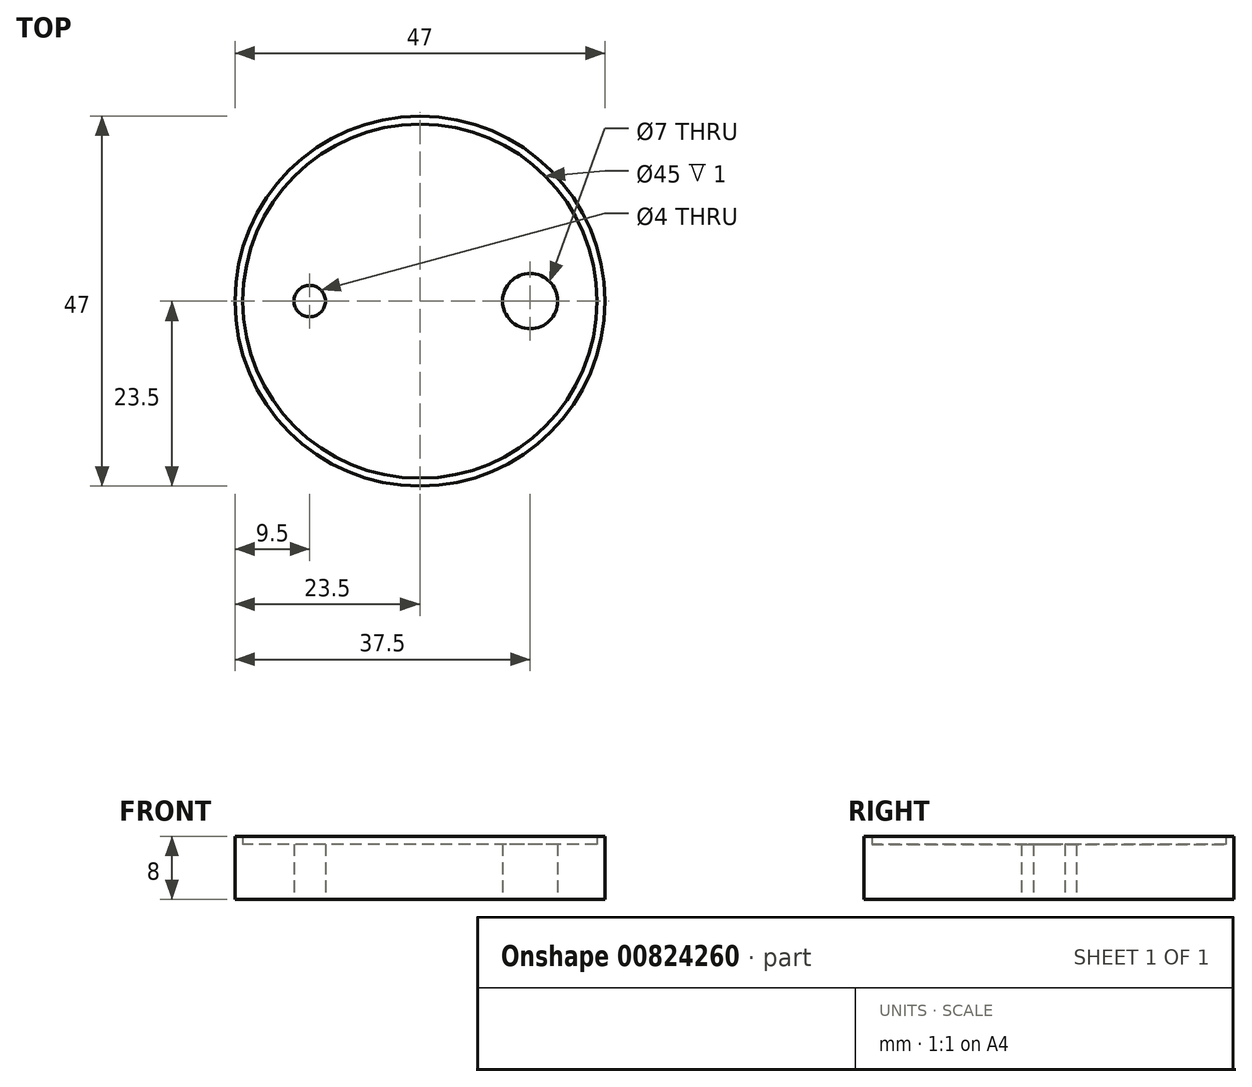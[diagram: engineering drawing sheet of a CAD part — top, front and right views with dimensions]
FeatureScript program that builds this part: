
annotation { "Feature Type Name" : "Feature", "Feature Type Description" : "" }
export const myFeature = defineFeature(function(context is Context, id is Id, definition is map)
    precondition{}
    {
        {
            var Q0;
            Q0=qCreatedBy(makeId("Top.planeOp"),FACE);
            var sketch = newSketch(context, id + "F0", { "sketchPlane" : qUnion([Q0])});
            skCircle(sketch, "E0", {"center": v(0, 0) * mm, "radius": 20 * mm});
            skCircle(sketch, "E1", {"center": v(0, 0) * mm, "radius": 22.5 * mm});
            skCircle(sketch, "E2", {"center": v(0, 0) * mm, "radius": 23.5 * mm});
            skPoint(sketch, "E3", {"position": v(-14, 0) * mm});
            skCircle(sketch, "E4", {"center": v(-14, 0) * mm, "radius": 3.5 * mm});
            skCircle(sketch, "E5.MirrorC", {"center": v(14, 0) * mm, "radius": 3.5 * mm});
            skLineSegment(sketch, "E6", {"start": v(-14, 3.5) * mm, "end": v(-19.7, 3.5) * mm});
            skLineSegment(sketch, "E7", {"start": v(-14, -3.5) * mm, "end": v(-19.7, -3.5) * mm});
            skLineSegment(sketch, "E8.MirrorCS", {"start": v(14, 3.5) * mm, "end": v(19.7, 3.5) * mm});
            skLineSegment(sketch, "E9.MirrorCS", {"start": v(14, -3.5) * mm, "end": v(19.7, -3.5) * mm});
            skSolve(sketch);
        }
        {
            var Q0;
            Q0=makeQuery(id+"F0.imprint","IMPRINT",FACE,{"disambiguationData":[TD([[makeQuery(id+"F0.imprint","IMPRINT",EDGE,{"derivedFrom":sQuery(id+"F0.wireOp",EDGE,"E1")}),1.0]])]});
            var Q1;
            {var subQ0=sQuery(id+"F0.wireOp",EDGE,"E6");Q1=makeQuery(id+"F0.imprint","IMPRINT",FACE,{"disambiguationData":[TD([[makeQuery(id+"F0.imprint","IMPRINT",EDGE,{"derivedFrom":subQ0}),1.0]])]});}
            var Q2;
            {var subQ0=sQuery(id+"F0.wireOp",EDGE,"E4");var subQ1=makeQuery(id+"F0.imprint","INTERSECT",VERTEX,{"derivedFrom":[subQ0,sQuery(id+"F0.wireOp",EDGE,"E6")]});Q2=makeQuery(id+"F0.imprint","IMPRINT",FACE,{"disambiguationData":[TD([[makeQuery(id+"F0.imprint","IMPRINT",EDGE,{"disambiguationData":[TD([[subQ1,-1.0]])],"derivedFrom":subQ0}),1.0]])]});}
            var Q3;
            {var subQ0=sQuery(id+"F0.wireOp",EDGE,"E5.MirrorC");var subQ1=makeQuery(id+"F0.imprint","INTERSECT",VERTEX,{"derivedFrom":[subQ0,sQuery(id+"F0.wireOp",EDGE,"E8.MirrorCS")]});Q3=makeQuery(id+"F0.imprint","IMPRINT",FACE,{"disambiguationData":[TD([[makeQuery(id+"F0.imprint","IMPRINT",EDGE,{"disambiguationData":[TD([[subQ1,-1.0]])],"derivedFrom":subQ0}),-1.0]])]});}
            var Q4;
            {var subQ0=sQuery(id+"F0.wireOp",EDGE,"E8.MirrorCS");Q4=makeQuery(id+"F0.imprint","IMPRINT",FACE,{"disambiguationData":[TD([[makeQuery(id+"F0.imprint","IMPRINT",EDGE,{"derivedFrom":subQ0}),-1.0]])]});}
            extrude(context, id + "F1", {"entities" : qUnion([Q0, Q1, Q2, Q3, Q4]), "depth" : 7 * mm, "offsetDistance" : 25 * mm});
        }
        {
            var Q0;
            Q0=makeQuery(id+"F0.imprint","IMPRINT",FACE,{"disambiguationData":[TD([[makeQuery(id+"F0.imprint","IMPRINT",EDGE,{"derivedFrom":sQuery(id+"F0.wireOp",EDGE,"E1")}),-1.0]])]});
            extrude(context, id + "F2", {"entities" : qUnion([Q0]), "operationType" : NewBodyOperationType.ADD, "depth" : 8 * mm, "offsetDistance" : 25 * mm});
        }
        {
            var Q0;
            Q0=sQuery(id+"F0.wireOp",VERTEX,"E3");
            var Q1;
            Q1=sQuery(id+"F0.wireOp",VERTEX,"E5.MirrorC.center");
            var Q2;
            Q2=makeQuery(id+"F1.opExtrude","SWEPT_BODY",BODY,{"disambiguationData":[OSD([sQuery(id+"F0.wireOp",EDGE,"E0"),sQuery(id+"F0.wireOp",EDGE,"E1"),sQuery(id+"F0.wireOp",EDGE,"E4"),sQuery(id+"F0.wireOp",EDGE,"E5.MirrorC"),sQuery(id+"F0.wireOp",EDGE,"E6"),sQuery(id+"F0.wireOp",EDGE,"E7"),sQuery(id+"F0.wireOp",EDGE,"E8.MirrorCS"),sQuery(id+"F0.wireOp",EDGE,"E9.MirrorCS")])]});
            hole(context, id + "F3", {"style" : HoleStyle.SIMPLE, "endStyle" : HoleEndStyle.THROUGH, "oppositeDirection" : true, "holeDiameter" : 4 * mm, "majorDiameter" : 5 * mm, "isTappedThrough" : true, "tappedDepth" : 12 * mm, "tapClearance" : 3, "locations" : qUnion([Q0, Q1]), "scope" : qUnion([Q2])});
        }
    });
